# Revit family: Standard Panel
name_source: partatom
category: Generic Models
revit_build: Autodesk Revit 2015 (Build: 20140606_1530(x64)
units: mm (PartAtom-declared; Revit-internal decimal feet)

## types (9) — shared parameters
Cut_Depth = -1' - 6"
Cut_Door_Right = No
D_R2_R3 = 1' - 0"
D_R3_R4 = 8' - 0"
D_R4_R5 = 1' - 0"
D_R_Right_CL_Side = 0' - 0"
D_To_Right_Door = 5' - 0"
D_Top_Reveal_To_CL_Modilion = 4' - 0"
Door_Cut_Calc_Right = -1' - 6"
Door_RO = 3' - 4"
End_Panel_Cut_Calc = 0' - 0"
Offset from Floor = -1' - 0"
Panel Depth = 0' - 8"
Window_Head_Reveal_Offset = 0' - 10"
Window_Jamb_Reveal_Offset = 0' - 8"

## per-type parameters (varying)
- 25' Window Side Entry: Chamfer_Right_Calc=0' - 0"; Chamfer_left_Calc=0' - 0"; Cut_Chamfer_Left=Yes; Cut_Chamfer_Right=Yes; Cut_Depth_Opp=0' - 0"; Cut_Door_Left=No; Cut_Entry_Left=No; Cut_Entry_Top=No; Cut_KO_Opening=No; Cut_Modillion=No; Cut_Window_Large_Reveal=Yes; Cut_Window_Opening=Yes; Cut_Window_Small_Reveal=No; D_Modilion_Off_center=0' - 0"; D_R1_R2=8' - 0"; D_R_Left_CL_Side=0' - 0"; D_To_Entry_Top_Curve_CL=0' - 0"; D_To_Left_door=7' - 6"; D_Top_R1=0' - 10"; Door_Cut_Calc_Left=-1' - 6"; Door_Height=10' - 0"; End_Panel=No; Entry_Cut_Left_Calc=-1' - 6"; Entry_Cut_Top_Calc=-1' - 6"; Hide_Top_Reveal=No; Modillion_Cut_Calc=-1' - 6"; Panel Height=39' - 0"; Panel Width=25' - 8"; Reveal_Top_Calc=0' - 0"; Widow_Dist_Left_from_center=7' - 10"; Widow_Dist_Right_from_center=7' - 2"; Window_Height=8' - 0"; Window_KO_Calc=-1' - 6"; Window_Reveal_Cut_Large_Calc=0' - 0"; Window_Reveal_Cut_Small_Calc=-1' - 6"; Window_Sill_Height=2' - 0"; Window_cut_Calc=0' - 0"
- 25' Window: Chamfer_Right_Calc=0' - 0"; Chamfer_left_Calc=0' - 0"; Cut_Chamfer_Left=Yes; Cut_Chamfer_Right=Yes; Cut_Depth_Opp=0' - 0"; Cut_Door_Left=No; Cut_Entry_Left=No; Cut_Entry_Top=No; Cut_KO_Opening=No; Cut_Modillion=No; Cut_Window_Large_Reveal=Yes; Cut_Window_Opening=Yes; Cut_Window_Small_Reveal=No; D_Modilion_Off_center=0' - 0"; D_R1_R2=8' - 0"; D_R_Left_CL_Side=0' - 0"; D_To_Entry_Top_Curve_CL=0' - 0"; D_To_Left_door=7' - 6"; D_Top_R1=0' - 10"; Door_Cut_Calc_Left=-1' - 6"; Door_Height=10' - 0"; End_Panel=No; Entry_Cut_Left_Calc=-1' - 6"; Entry_Cut_Top_Calc=-1' - 6"; Hide_Top_Reveal=No; Modillion_Cut_Calc=-1' - 6"; Panel Height=39' - 0"; Panel Width=25' - 0"; Reveal_Top_Calc=0' - 0"; Widow_Dist_Left_from_center=7' - 6"; Widow_Dist_Right_from_center=7' - 6"; Window_Height=8' - 0"; Window_KO_Calc=-1' - 6"; Window_Reveal_Cut_Large_Calc=0' - 0"; Window_Reveal_Cut_Small_Calc=-1' - 6"; Window_Sill_Height=2' - 0"; Window_cut_Calc=0' - 0"
- 25' KO Door Left: Chamfer_Right_Calc=0' - 0"; Chamfer_left_Calc=0' - 0"; Cut_Chamfer_Left=Yes; Cut_Chamfer_Right=Yes; Cut_Depth_Opp=0' - 0"; Cut_Door_Left=Yes; Cut_Entry_Left=No; Cut_Entry_Top=No; Cut_KO_Opening=Yes; Cut_Modillion=No; Cut_Window_Large_Reveal=No; Cut_Window_Opening=No; Cut_Window_Small_Reveal=No; D_Modilion_Off_center=0' - 0"; D_R1_R2=8' - 0"; D_R_Left_CL_Side=0' - 0"; D_To_Entry_Top_Curve_CL=0' - 0"; D_To_Left_door=7' - 6"; D_Top_R1=0' - 10"; Door_Cut_Calc_Left=0' - 0"; Door_Height=10' - 0"; End_Panel=No; Entry_Cut_Left_Calc=-1' - 6"; Entry_Cut_Top_Calc=-1' - 6"; Hide_Top_Reveal=No; Modillion_Cut_Calc=-1' - 6"; Panel Height=39' - 0"; Panel Width=25' - 0"; Reveal_Top_Calc=0' - 0"; Widow_Dist_Left_from_center=7' - 6"; Widow_Dist_Right_from_center=7' - 6"; Window_Height=8' - 0"; Window_KO_Calc=0' - 0"; Window_Reveal_Cut_Large_Calc=-1' - 6"; Window_Reveal_Cut_Small_Calc=-1' - 6"; Window_Sill_Height=2' - 0"; Window_cut_Calc=-1' - 6"
- 25' KO: Chamfer_Right_Calc=0' - 0"; Chamfer_left_Calc=0' - 0"; Cut_Chamfer_Left=Yes; Cut_Chamfer_Right=Yes; Cut_Depth_Opp=0' - 0"; Cut_Door_Left=No; Cut_Entry_Left=No; Cut_Entry_Top=No; Cut_KO_Opening=Yes; Cut_Modillion=No; Cut_Window_Large_Reveal=No; Cut_Window_Opening=No; Cut_Window_Small_Reveal=No; D_Modilion_Off_center=0' - 0"; D_R1_R2=8' - 0"; D_R_Left_CL_Side=0' - 0"; D_To_Entry_Top_Curve_CL=0' - 0"; D_To_Left_door=7' - 6"; D_Top_R1=0' - 10"; Door_Cut_Calc_Left=-1' - 6"; Door_Height=8' - 0"; End_Panel=No; Entry_Cut_Left_Calc=-1' - 6"; Entry_Cut_Top_Calc=-1' - 6"; Hide_Top_Reveal=No; Modillion_Cut_Calc=-1' - 6"; Panel Height=39' - 0"; Panel Width=25' - 0"; Reveal_Top_Calc=0' - 0"; Widow_Dist_Left_from_center=7' - 6"; Widow_Dist_Right_from_center=7' - 6"; Window_Height=8' - 0"; Window_KO_Calc=0' - 0"; Window_Reveal_Cut_Large_Calc=-1' - 6"; Window_Reveal_Cut_Small_Calc=-1' - 6"; Window_Sill_Height=2' - 0"; Window_cut_Calc=-1' - 6"
- 8' Corner: Chamfer_Right_Calc=0' - 0"; Chamfer_left_Calc=0' - 0"; Cut_Chamfer_Left=Yes; Cut_Chamfer_Right=Yes; Cut_Depth_Opp=1' - 6"; Cut_Door_Left=No; Cut_Entry_Left=No; Cut_Entry_Top=No; Cut_KO_Opening=No; Cut_Modillion=Yes; Cut_Window_Large_Reveal=No; Cut_Window_Opening=No; Cut_Window_Small_Reveal=No; D_Modilion_Off_center=0' - 0"; D_R1_R2=8' - 0"; D_R_Left_CL_Side=0' - 0"; D_To_Entry_Top_Curve_CL=0' - 0"; D_To_Left_door=5' - 0"; D_Top_R1=0' - 10"; Door_Cut_Calc_Left=-1' - 6"; Door_Height=8' - 0"; End_Panel=Yes; Entry_Cut_Left_Calc=-1' - 6"; Entry_Cut_Top_Calc=-1' - 6"; Hide_Top_Reveal=No; Modillion_Cut_Calc=0' - 0"; Panel Height=39' - 0"; Panel Width=8' - 0"; Reveal_Top_Calc=0' - 0"; Widow_Dist_Left_from_center=7' - 6"; Widow_Dist_Right_from_center=7' - 6"; Window_Height=8' - 0"; Window_KO_Calc=-1' - 6"; Window_Reveal_Cut_Large_Calc=-1' - 6"; Window_Reveal_Cut_Small_Calc=-1' - 6"; Window_Sill_Height=2' - 0"; Window_cut_Calc=-1' - 6"
- 12'-6" Side Entry Left: Chamfer_Right_Calc=0' - 0"; Chamfer_left_Calc=-1' - 6"; Cut_Chamfer_Left=No; Cut_Chamfer_Right=Yes; Cut_Depth_Opp=0' - 0"; Cut_Door_Left=No; Cut_Entry_Left=Yes; Cut_Entry_Top=Yes; Cut_KO_Opening=Yes; Cut_Modillion=Yes; Cut_Window_Large_Reveal=No; Cut_Window_Opening=Yes; Cut_Window_Small_Reveal=Yes; D_Modilion_Off_center=0' - 7"; D_R1_R2=9' - 0"; D_R_Left_CL_Side=1' - 1"; D_To_Entry_Top_Curve_CL=0' - 7 1/2"; D_To_Left_door=7' - 6"; D_Top_R1=1' - 3 1/2"; Door_Cut_Calc_Left=-1' - 6"; Door_Height=8' - 0"; End_Panel=No; Entry_Cut_Left_Calc=0' - 0"; Entry_Cut_Top_Calc=0' - 0"; Hide_Top_Reveal=Yes; Modillion_Cut_Calc=0' - 0"; Panel Height=40' - 5"; Panel Width=12' - 6"; Reveal_Top_Calc=-1' - 6"; Widow_Dist_Left_from_center=3' - 2"; Widow_Dist_Right_from_center=4' - 4"; Window_Height=8' - 0"; Window_KO_Calc=0' - 0"; Window_Reveal_Cut_Large_Calc=-1' - 6"; Window_Reveal_Cut_Small_Calc=0' - 0"; Window_Sill_Height=2' - 0"; Window_cut_Calc=0' - 0"
- 25' Entry: Chamfer_Right_Calc=0' - 0"; Chamfer_left_Calc=0' - 0"; Cut_Chamfer_Left=Yes; Cut_Chamfer_Right=Yes; Cut_Depth_Opp=0' - 0"; Cut_Door_Left=No; Cut_Entry_Left=No; Cut_Entry_Top=Yes; Cut_KO_Opening=Yes; Cut_Modillion=Yes; Cut_Window_Large_Reveal=No; Cut_Window_Opening=Yes; Cut_Window_Small_Reveal=No; D_Modilion_Off_center=0' - 0"; D_R1_R2=9' - 0"; D_R_Left_CL_Side=0' - 0"; D_To_Entry_Top_Curve_CL=0' - 7 1/2"; D_To_Left_door=7' - 6"; D_Top_R1=1' - 3 1/2"; Door_Cut_Calc_Left=-1' - 6"; Door_Height=8' - 0"; End_Panel=No; Entry_Cut_Left_Calc=-1' - 6"; Entry_Cut_Top_Calc=0' - 0"; Hide_Top_Reveal=No; Modillion_Cut_Calc=0' - 0"; Panel Height=40' - 5"; Panel Width=25' - 0"; Reveal_Top_Calc=0' - 0"; Widow_Dist_Left_from_center=10' - 0"; Widow_Dist_Right_from_center=10' - 0"; Window_Height=10' - 0"; Window_KO_Calc=0' - 0"; Window_Reveal_Cut_Large_Calc=-1' - 6"; Window_Reveal_Cut_Small_Calc=-1' - 6"; Window_Sill_Height=0' - 0"; Window_cut_Calc=0' - 0"
- 22'' panel: Chamfer_Right_Calc=-1' - 6"; Chamfer_left_Calc=-1' - 6"; Cut_Chamfer_Left=No; Cut_Chamfer_Right=No; Cut_Depth_Opp=0' - 0"; Cut_Door_Left=No; Cut_Entry_Left=No; Cut_Entry_Top=Yes; Cut_KO_Opening=No; Cut_Modillion=Yes; Cut_Window_Large_Reveal=No; Cut_Window_Opening=No; Cut_Window_Small_Reveal=No; D_Modilion_Off_center=0' - 0"; D_R1_R2=8' - 0"; D_R_Left_CL_Side=0' - 0"; D_To_Entry_Top_Curve_CL=0' - 7 1/2"; D_To_Left_door=5' - 0"; D_Top_R1=0' - 10"; Door_Cut_Calc_Left=-1' - 6"; Door_Height=8' - 0"; End_Panel=No; Entry_Cut_Left_Calc=-1' - 6"; Entry_Cut_Top_Calc=0' - 0"; Hide_Top_Reveal=No; Modillion_Cut_Calc=0' - 0"; Panel Height=39' - 0"; Panel Width=22' - 0"; Reveal_Top_Calc=0' - 0"; Widow_Dist_Left_from_center=7' - 6"; Widow_Dist_Right_from_center=7' - 6"; Window_Height=8' - 0"; Window_KO_Calc=-1' - 6"; Window_Reveal_Cut_Large_Calc=-1' - 6"; Window_Reveal_Cut_Small_Calc=-1' - 6"; Window_Sill_Height=2' - 0"; Window_cut_Calc=-1' - 6"
- 24'-4" KO: Chamfer_Right_Calc=0' - 0"; Chamfer_left_Calc=0' - 0"; Cut_Chamfer_Left=Yes; Cut_Chamfer_Right=Yes; Cut_Depth_Opp=0' - 0"; Cut_Door_Left=No; Cut_Entry_Left=No; Cut_Entry_Top=No; Cut_KO_Opening=Yes; Cut_Modillion=No; Cut_Window_Large_Reveal=No; Cut_Window_Opening=No; Cut_Window_Small_Reveal=No; D_Modilion_Off_center=0' - 0"; D_R1_R2=8' - 0"; D_R_Left_CL_Side=0' - 0"; D_To_Entry_Top_Curve_CL=0' - 0"; D_To_Left_door=7' - 6"; D_Top_R1=0' - 10"; Door_Cut_Calc_Left=-1' - 6"; Door_Height=8' - 0"; End_Panel=No; Entry_Cut_Left_Calc=-1' - 6"; Entry_Cut_Top_Calc=-1' - 6"; Hide_Top_Reveal=No; Modillion_Cut_Calc=-1' - 6"; Panel Height=39' - 0"; Panel Width=24' - 4"; Reveal_Top_Calc=0' - 0"; Widow_Dist_Left_from_center=7' - 2"; Widow_Dist_Right_from_center=7' - 10"; Window_Height=8' - 0"; Window_KO_Calc=0' - 0"; Window_Reveal_Cut_Large_Calc=-1' - 6"; Window_Reveal_Cut_Small_Calc=-1' - 6"; Window_Sill_Height=2' - 0"; Window_cut_Calc=-1' - 6"

## geometry (parser evidence)
native form markers: Blend x4, Sweep x6
no freeform markers — native parametric forms only
